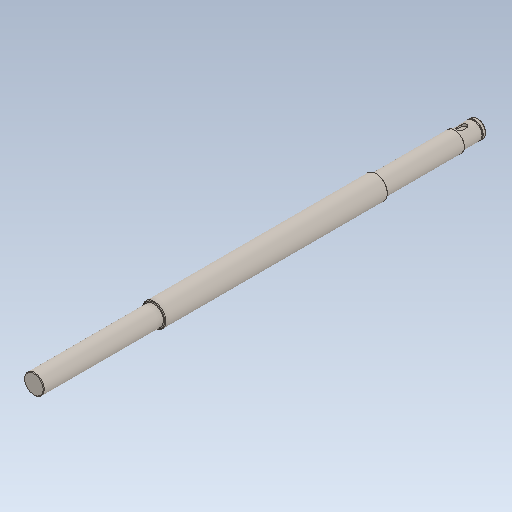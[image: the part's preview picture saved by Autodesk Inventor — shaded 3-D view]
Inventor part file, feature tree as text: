
AUTODESK INVENTOR PART (.ipt)
format: ipt  version: 2021 (Build 250183000, 183)  size: 114,688 bytes
history: mixed  units: mm
features: other x1, chamfer x1, imported_body x1
ambient origin geometry x8: Origin, YZ Plane, XZ Plane, XY Plane, X Axis, Y Axis, Z Axis, Center Point
bodies: Body1 (imported_parasolid)
feature tree (3):
  other  "Sólido1"
  chamfer  "Chamfer2"  [1 undecoded]
  imported_body  NMx_Import_Brep_tag  [imported B-rep: ~21 faces, bbox_mm=[18.5, 0.0, 381.0]]
note: 1 required parameter value undecoded (feature->parameter linkage not recoverable at this tier; creation-order binding heuristic only, values carry confidence <= 0.55)
